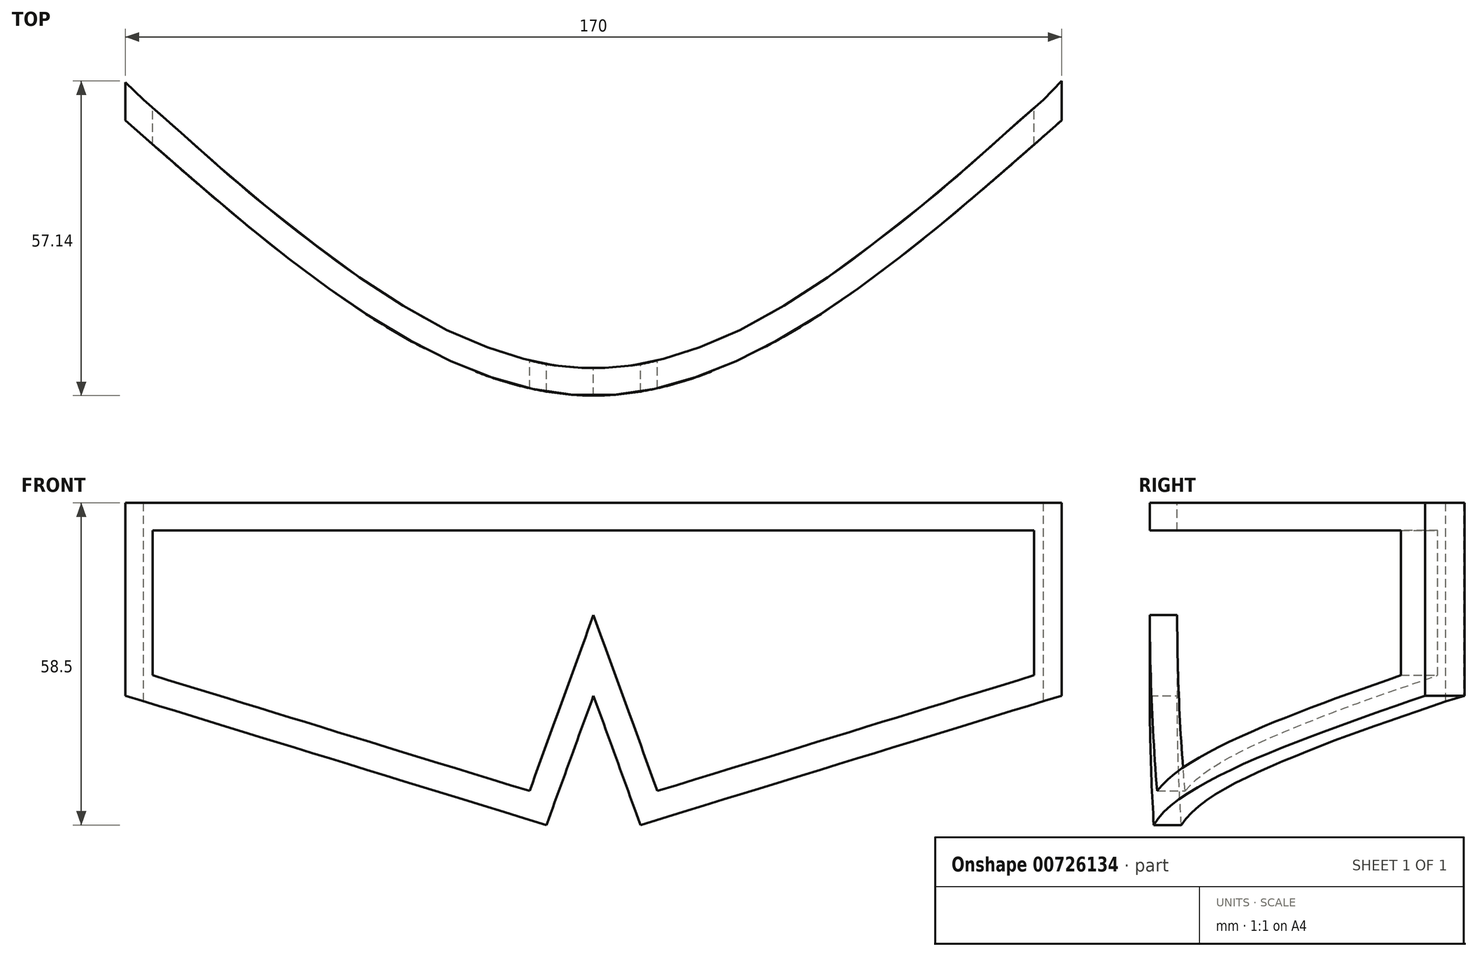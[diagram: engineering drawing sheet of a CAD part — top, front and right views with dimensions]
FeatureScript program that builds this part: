
annotation { "Feature Type Name" : "Feature", "Feature Type Description" : "" }
export const myFeature = defineFeature(function(context is Context, id is Id, definition is map)
    precondition{}
    {
        {
            var Q0;
            Q0=qCreatedBy(makeId("Front.planeOp"),FACE);
            var sketch = newSketch(context, id + "F0", { "sketchPlane" : qUnion([Q0])});
            skLineSegment(sketch, "E0.top", {"start": v(-6.43, 59.8) * mm, "end": v(-91.43, 59.8) * mm});
            skLineSegment(sketch, "E0.right", {"start": v(-91.43, 24.8) * mm, "end": v(-91.43, 59.8) * mm});
            skLineSegment(sketch, "E1", {"start": v(-14.96, 1.3) * mm, "end": v(-6.43, 24.8) * mm});
            skLineSegment(sketch, "E2", {"start": v(-14.96, 1.3) * mm, "end": v(-91.43, 24.8) * mm});
            skLineSegment(sketch, "E3.MirrorCS", {"start": v(2.1, 1.3) * mm, "end": v(-6.43, 24.8) * mm});
            skLineSegment(sketch, "E4.MirrorCS", {"start": v(2.1, 1.3) * mm, "end": v(78.57, 24.8) * mm});
            skLineSegment(sketch, "E5.MirrorCS", {"start": v(78.57, 24.8) * mm, "end": v(78.57, 59.8) * mm});
            skLineSegment(sketch, "E6.MirrorCS", {"start": v(-6.43, 59.8) * mm, "end": v(78.57, 59.8) * mm});
            skLineSegment(sketch, "E7.0", {"start": v(-6.43, 54.8) * mm, "end": v(-86.43, 54.8) * mm});
            skLineSegment(sketch, "E7.1", {"start": v(-86.43, 28.5) * mm, "end": v(-86.43, 54.8) * mm});
            skLineSegment(sketch, "E7.2", {"start": v(-6.43, 54.8) * mm, "end": v(73.57, 54.8) * mm});
            skLineSegment(sketch, "E7.3", {"start": v(-18.03, 7.48) * mm, "end": v(-86.43, 28.5) * mm});
            skLineSegment(sketch, "E7.4", {"start": v(73.57, 28.5) * mm, "end": v(73.57, 54.8) * mm});
            skLineSegment(sketch, "E7.5", {"start": v(5.18, 7.48) * mm, "end": v(73.57, 28.5) * mm});
            skLineSegment(sketch, "E7.6", {"start": v(5.18, 7.48) * mm, "end": v(-6.43, 39.46) * mm});
            skLineSegment(sketch, "E7.7", {"start": v(-18.03, 7.48) * mm, "end": v(-6.43, 39.46) * mm});
            skSolve(sketch);
        }
        {
            var Q0;
            Q0=makeQuery(id+"F0.imprint","IMPRINT",FACE,{"disambiguationData":[TD([[makeQuery(id+"F0.imprint","IMPRINT",EDGE,{"derivedFrom":sQuery(id+"F0.wireOp",EDGE,"E0.top")}),1.0]])]});
            extrude(context, id + "F1", {"entities" : qUnion([Q0]), "depth" : 100 * mm, "offsetDistance" : 25 * mm});
        }
        {
            var Q0;
            Q0=makeQuery(id+"F1.opExtrude","SWEPT_FACE",FACE,{"disambiguationData":[OSD([sQuery(id+"F0.wireOp",EDGE,"E0.top"),sQuery(id+"F0.wireOp",EDGE,"E6.MirrorCS")])]});
            var sketch = newSketch(context, id + "F2", { "sketchPlane" : qUnion([Q0])});
            skFitSpline(sketch, "E8", {"points": [v(-91.43, -50) * mm, v(-6.43, -100) * mm, v(78.57, -50) * mm], "startDerivative": vector(170, -150) * mm, "endDerivative": vector(170, 150) * mm});
            skFitSpline(sketch, "E9.0", {"points": [v(-88.12, -46.25) * mm, v(-81.04, -52.5) * mm, v(-70.47, -61.82) * mm, v(-56.52, -72.98) * mm, v(-46.15, -80.4) * mm, v(-35.9, -86.62) * mm, v(-27.52, -90.54) * mm, v(-20.92, -92.82) * mm, v(-16.03, -94.06) * mm, v(-12, -94.7) * mm, v(-8.81, -94.96) * mm, v(-6.43, -95.02) * mm, v(-4.04, -94.96) * mm, v(-0.85, -94.7) * mm, v(3.18, -94.06) * mm, v(8.06, -92.82) * mm, v(14.66, -90.54) * mm, v(23.05, -86.62) * mm, v(33.3, -80.4) * mm, v(43.66, -72.98) * mm, v(57.61, -61.82) * mm, v(68.18, -52.5) * mm, v(75.26, -46.25) * mm]});
            skLineSegment(sketch, "E10", {"start": v(83.2, -38.12) * mm, "end": v(86.76, -41.6) * mm});
            skLineSegment(sketch, "E11", {"start": v(-103.28, -39.2) * mm, "end": v(-99.5, -35.28) * mm});
            skLineSegment(sketch, "E12", {"start": v(78.57, -50) * mm, "end": v(86.76, -41.6) * mm});
            skLineSegment(sketch, "E13", {"start": v(75.26, -46.25) * mm, "end": v(83.2, -38.12) * mm});
            skLineSegment(sketch, "E14", {"start": v(-91.43, -50) * mm, "end": v(-103.28, -39.2) * mm});
            skLineSegment(sketch, "E15", {"start": v(-88.12, -46.25) * mm, "end": v(-99.5, -35.28) * mm});
            skSolve(sketch);
        }
        {
            var Q0;
            Q0 = qSketchRegion(id + "F2", true);
            extrude(context, id + "F3", {"entities" : qUnion([Q0]), "operationType" : NewBodyOperationType.INTERSECT, "oppositeDirection" : true, "depth" : 70 * mm, "offsetDistance" : 25 * mm});
        }
    });
